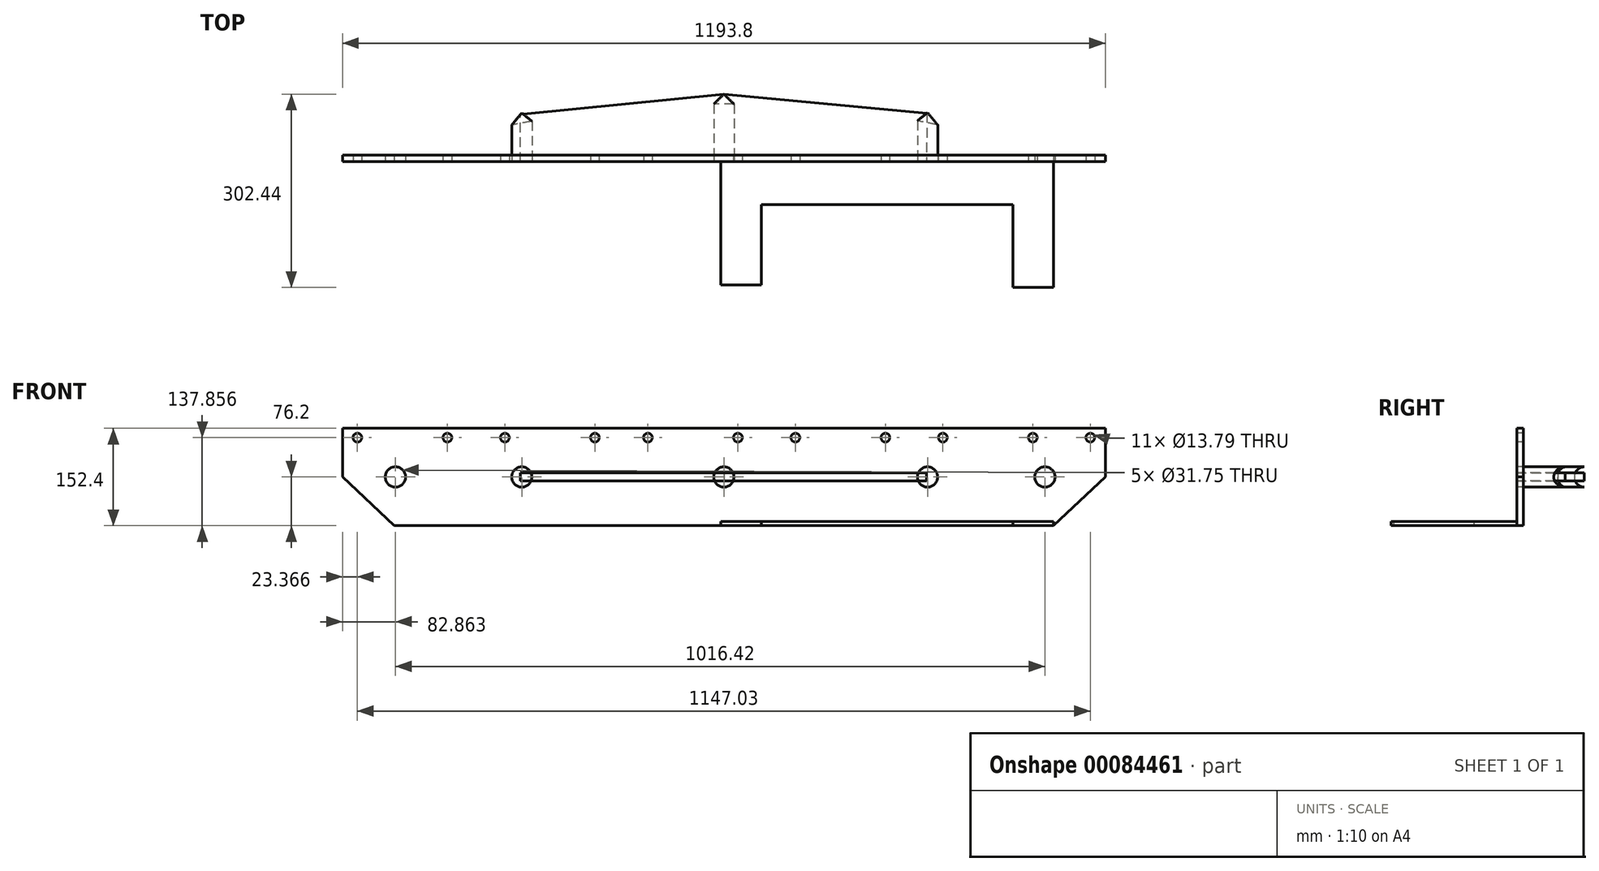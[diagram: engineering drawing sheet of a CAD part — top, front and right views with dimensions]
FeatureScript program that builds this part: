
annotation { "Feature Type Name" : "Feature", "Feature Type Description" : "" }
export const myFeature = defineFeature(function(context is Context, id is Id, definition is map)
    precondition{}
    {
        {
            var Q0;
            Q0=qCreatedBy(makeId("Top.planeOp"),FACE);
            var sketch = newSketch(context, id + "F0", { "sketchPlane" : qUnion([Q0])});
            skPoint(sketch, "E0.end.orphan", {"position": v(-514.04, 0) * mm});
            skPoint(sketch, "E1.start.orphan", {"position": v(501.96, 0) * mm});
            skFitSpline(sketch, "E2", {"points": [v(-514.04, 0) * mm, v(0, 105.24) * mm, v(501.96, 0) * mm], "startDerivative": vector(102.11, 285.12) * mm, "endDerivative": vector(70.62, -311.42) * mm});
            skSolve(sketch);
        }
        {
            var Q0;
            Q0=qCreatedBy(makeId("Front.planeOp"),FACE);
            var sketch = newSketch(context, id + "F1", { "sketchPlane" : qUnion([Q0])});
            skCircle(sketch, "E3", {"center": v(-514.04, 0) * mm, "radius": 15.88 * mm});
            skLineSegment(sketch, "E4.bottom", {"start": v(-516.14, -76.2) * mm, "end": v(516.14, -76.2) * mm});
            skLineSegment(sketch, "E4.top", {"start": v(-596.9, 76.2) * mm, "end": v(596.9, 76.2) * mm});
            skLineSegment(sketch, "E4.left", {"start": v(-596.9, 0) * mm, "end": v(-596.9, 76.2) * mm});
            skLineSegment(sketch, "E4.right", {"start": v(596.9, 0) * mm, "end": v(596.9, 76.2) * mm});
            skPoint(sketch, "E4.middle", {"position": v(0, 0) * mm});
            skLineSegment(sketch, "E5", {"start": v(596.9, 0) * mm, "end": v(516.14, -76.2) * mm});
            skPoint(sketch, "E6.orphan", {"position": v(596.9, -76.2) * mm});
            skLineSegment(sketch, "E7", {"start": v(-596.9, 0) * mm, "end": v(-516.14, -76.2) * mm});
            skPoint(sketch, "E8.orphan", {"position": v(-596.9, -76.2) * mm});
            skCircle(sketch, "E9", {"center": v(318.68, 0) * mm, "radius": 15.88 * mm});
            skCircle(sketch, "E10", {"center": v(-316.32, 0) * mm, "radius": 15.88 * mm});
            skCircle(sketch, "E11", {"center": v(0, 0) * mm, "radius": 15.88 * mm});
            skCircle(sketch, "E12", {"center": v(502.39, 0) * mm, "radius": 15.88 * mm});
            skCircle(sketch, "E13", {"center": v(573.5, 61.66) * mm, "radius": 6.9 * mm});
            skLineSegment(sketch, "E14", {"start": v(573.5, 61.66) * mm, "end": v(-811.21, 61.66) * mm});
            skCircle(sketch, "E15", {"center": v(-811.21, 61.66) * mm, "radius": 6.9 * mm});
            skCircle(sketch, "E16", {"center": v(483.5, 61.66) * mm, "radius": 6.9 * mm});
            skCircle(sketch, "E17", {"center": v(342.7, 61.66) * mm, "radius": 6.9 * mm});
            skCircle(sketch, "E18", {"center": v(252.72, 61.66) * mm, "radius": 6.9 * mm});
            skCircle(sketch, "E19", {"center": v(111.92, 61.66) * mm, "radius": 6.9 * mm});
            skCircle(sketch, "E20", {"center": v(21.93, 61.66) * mm, "radius": 6.9 * mm});
            skCircle(sketch, "E21", {"center": v(-118.86, 61.66) * mm, "radius": 6.9 * mm});
            skCircle(sketch, "E22", {"center": v(-201.96, 61.66) * mm, "radius": 6.9 * mm});
            skCircle(sketch, "E23", {"center": v(-342.75, 61.66) * mm, "radius": 6.9 * mm});
            skCircle(sketch, "E24", {"center": v(-432.74, 61.66) * mm, "radius": 6.9 * mm});
            skCircle(sketch, "E25", {"center": v(-573.53, 61.66) * mm, "radius": 6.9 * mm});
            skSolve(sketch);
        }
        {
            var Q0;
            Q0=makeQuery(id+"F1.imprint","IMPRINT",FACE,{"disambiguationData":[TD([[makeQuery(id+"F1.imprint","IMPRINT",EDGE,{"derivedFrom":sQuery(id+"F1.wireOp",EDGE,"E12")}),1.0]])]});
            var Q1;
            Q1=sQuery(id+"F1.wireOp",EDGE,"E12");
            var Q2;
            Q2=sQuery(id+"F0.wireOp",EDGE,"E2");
            sweep(context, id + "F2", {"bodyType" : ToolBodyType.SURFACE, "profiles" : qUnion([Q0]), "surfaceProfiles" : qUnion([Q1]), "path" : qUnion([Q2])});
        }
        {
            var Q0;
            Q0=makeQuery(id+"F1.imprint","IMPRINT",FACE,{"disambiguationData":[TD([[makeQuery(id+"F1.imprint","IMPRINT",EDGE,{"derivedFrom":sQuery(id+"F1.wireOp",EDGE,"E10")}),1.0]])]});
            var Q1;
            Q1=makeQuery(id+"F1.imprint","IMPRINT",FACE,{"disambiguationData":[TD([[makeQuery(id+"F1.imprint","IMPRINT",EDGE,{"derivedFrom":sQuery(id+"F1.wireOp",EDGE,"E11")}),1.0]])]});
            var Q2;
            Q2=makeQuery(id+"F1.imprint","IMPRINT",FACE,{"disambiguationData":[TD([[makeQuery(id+"F1.imprint","IMPRINT",EDGE,{"derivedFrom":sQuery(id+"F1.wireOp",EDGE,"E9")}),1.0]])]});
            var Q3;
            Q3=makeQuery(id+"F2.opSweep","SWEPT_FACE",FACE,{"disambiguationData":[OSD([sQuery(id+"F0.wireOp",EDGE,"E2"),sQuery(id+"F1.wireOp",EDGE,"E12")])]});
            var Q4;
            Q4=makeQuery(id+"F2.opSweep","SWEPT_BODY",BODY,{"disambiguationData":[OSD([sQuery(id+"F0.wireOp",EDGE,"E2"),sQuery(id+"F1.wireOp",EDGE,"E12")])]});
            extrude(context, id + "F3", {"entities" : qUnion([Q0, Q1, Q2]), "endBound" : BoundingType.UP_TO_SURFACE, "oppositeDirection" : true, "endBoundEntityFace" : qUnion([Q3]), "depth" : 101.6 * mm});
        }
        {
            var Q0;
            Q0=makeQuery(id+"F1.imprint","IMPRINT",FACE,{"disambiguationData":[TD([[makeQuery(id+"F1.imprint","IMPRINT",EDGE,{"derivedFrom":sQuery(id+"F1.wireOp",EDGE,"E3")}),-1.0]])]});
            var Q1;
            Q1=sQuery(id+"F1.wireOp",EDGE,"E4.top");
            var Q2;
            Q2=sQuery(id+"F1.wireOp",EDGE,"E4.bottom");
            var Q3;
            Q3=sQuery(id+"F1.wireOp",EDGE,"E5");
            var Q4;
            Q4=sQuery(id+"F1.wireOp",EDGE,"E7");
            var Q5;
            Q5=sQuery(id+"F1.wireOp",EDGE,"E4.left");
            var Q6;
            Q6=sQuery(id+"F1.wireOp",EDGE,"E3");
            var Q7;
            Q7=sQuery(id+"F1.wireOp",EDGE,"E10");
            var Q8;
            Q8=sQuery(id+"F1.wireOp",EDGE,"E11");
            var Q9;
            Q9=sQuery(id+"F1.wireOp",EDGE,"E9");
            var Q10;
            Q10=sQuery(id+"F1.wireOp",EDGE,"E12");
            var Q11;
            Q11=sQuery(id+"F1.wireOp",EDGE,"E4.right");
            extrude(context, id + "F4", {"entities" : qUnion([Q0]), "surfaceEntities" : qUnion([Q1, Q2, Q3, Q4, Q5, Q6, Q7, Q8, Q9, Q10, Q11]), "oppositeDirection" : true, "depth" : 10.16 * mm});
        }
        {
            var Q0;
            Q0=qCreatedBy(makeId("Top.planeOp"),FACE);
            var sketch = newSketch(context, id + "F5", { "sketchPlane" : qUnion([Q0])});
            skLineSegment(sketch, "E26", {"start": v(317.06, 0) * mm, "end": v(-318.7, 0) * mm});
            skLineSegment(sketch, "E27", {"start": v(-318.7, 0) * mm, "end": v(-318.7, 74.14) * mm});
            skLineSegment(sketch, "E28", {"start": v(-318.7, 74.14) * mm, "end": v(0, 105.28) * mm});
            skLineSegment(sketch, "E29", {"start": v(0, 105.28) * mm, "end": v(317.88, 75.78) * mm});
            skLineSegment(sketch, "E30", {"start": v(317.88, 75.78) * mm, "end": v(317.06, 0) * mm});
            skSolve(sketch);
        }
        {
            var Q0;
            Q0 = qSketchRegion(id + "F5", true);
            extrude(context, id + "F6", {"entities" : qUnion([Q0]), "endBound" : BoundingType.SYMMETRIC, "depth" : 12.7 * mm});
        }
        {
            var Q0;
            Q0=makeQuery(id+"F4.opExtrude","SWEPT_FACE",FACE,{"disambiguationData":[OSD([sQuery(id+"F1.wireOp",EDGE,"E4.bottom")])]});
            var sketch = newSketch(context, id + "F7", { "sketchPlane" : qUnion([Q0])});
            skLineSegment(sketch, "E31", {"start": v(516.14, -10.16) * mm, "end": v(516.14, 196.8) * mm});
            skLineSegment(sketch, "E32", {"start": v(516.14, 196.8) * mm, "end": v(452.64, 196.8) * mm});
            skLineSegment(sketch, "E33", {"start": v(452.64, 196.8) * mm, "end": v(452.64, 67.25) * mm});
            skLineSegment(sketch, "E34", {"start": v(452.64, 67.25) * mm, "end": v(58.94, 67.25) * mm});
            skLineSegment(sketch, "E35", {"start": v(58.94, 67.25) * mm, "end": v(58.94, 193.04) * mm});
            skLineSegment(sketch, "E36", {"start": v(58.94, 193.04) * mm, "end": v(-4.56, 193.04) * mm});
            skLineSegment(sketch, "E37", {"start": v(-4.56, 193.04) * mm, "end": v(-4.56, -10.16) * mm});
            skLineSegment(sketch, "E38", {"start": v(-4.56, -10.16) * mm, "end": v(516.14, -10.16) * mm});
            skSolve(sketch);
        }
        {
            var Q0;
            Q0 = qSketchRegion(id + "F7", true);
            extrude(context, id + "F8", {"entities" : qUnion([Q0]), "operationType" : NewBodyOperationType.ADD, "oppositeDirection" : true, "depth" : 6.35 * mm});
        }
    });
